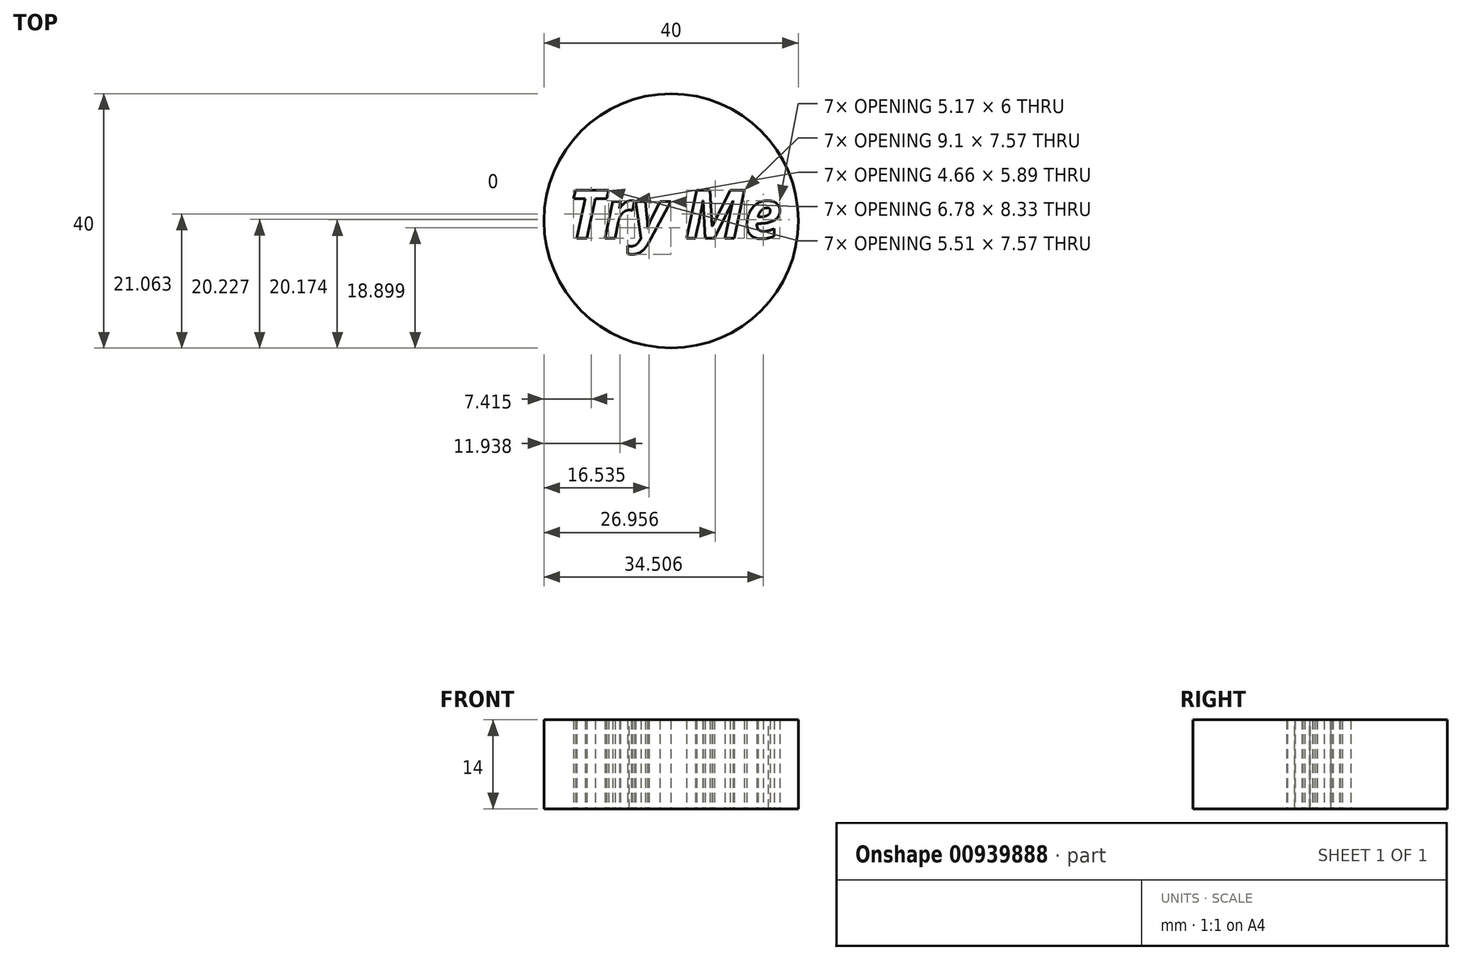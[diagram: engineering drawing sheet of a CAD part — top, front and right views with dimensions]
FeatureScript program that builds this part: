
annotation { "Feature Type Name" : "Feature", "Feature Type Description" : "" }
export const myFeature = defineFeature(function(context is Context, id is Id, definition is map)
    precondition{}
    {
        {
            var Q0;
            Q0=qCreatedBy(makeId("Top.planeOp"),FACE);
            var sketch = newSketch(context, id + "F0", { "sketchPlane" : qUnion([Q0])});
            skCircle(sketch, "E0", {"center": v(0, 0) * mm, "radius": 20 * mm});
            skSolve(sketch);
        }
        {
            var Q0;
            Q0 = qSketchRegion(id + "F0", true);
            extrude(context, id + "F1", {"entities" : qUnion([Q0]), "depth" : 14 * mm, "offsetDistance" : 25.4 * mm});
        }
        {
            var Q0;
            Q0=qCreatedBy(makeId("Top.planeOp"),FACE);
            var sketch = newSketch(context, id + "F2", { "sketchPlane" : qUnion([Q0])});
            skText(sketch, "E1", { "text": "Try Me", "fontName": "OpenSans-BoldItalic.ttf"});
            const initialGuessF2  = {"E1": [-0.01621, -0.00272, 1, 0, 0.00763]};
            skSetInitialGuess(sketch, initialGuessF2);
            skSolve(sketch);
        }
        {
            var Q0;
            Q0 = qSketchRegion(id + "F2", true);
            extrude(context, id + "F3", {"entities" : qUnion([Q0]), "operationType" : NewBodyOperationType.REMOVE, "depth" : 35.3 * mm, "offsetDistance" : 25.4 * mm});
        }
    });
